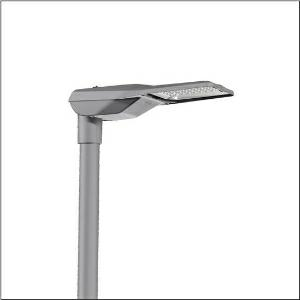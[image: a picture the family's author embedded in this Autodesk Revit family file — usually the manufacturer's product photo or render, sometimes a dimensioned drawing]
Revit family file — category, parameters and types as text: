
# Revit family: streetlight_sl_21_iq_mini___p0_8a_5xe2u31v08hb_1f16
name_source: partatom
category: Lighting Fixtures
units: mm (PartAtom-declared; Revit-internal decimal feet)

## family parameters
Cut with Voids When Loaded = No
Host = Face
Light Source = No
Part Type = Normal
Room Calculation Point = No
Round Connector Dimension = Use Diameter
Shared = No

## types (1)
- --- (1 x LED, 9830 lm, 71 W, 3000K)
    Apparent Load = 71 VA
    CIE Flux Codes = 33 69 96 100 100
    Color Rendering = 70
    Color Temperature = 3000K
    Default Elevation = 1800 mm
    Description = Streetlight SL 21 iQ mini, mast luminaire, primary light control with lens, of PMMA, primary optical cover: cover, of toughened safety glass, transparent, light distribution: P0.8a, light emission: direct distribution, primary light characteristic: asymmetric, installation type: post-top, side-entry, LED, High Power LED, rated luminous flux: 9.830lm, luminous efficacy: 139lm/W, light colour: 730, colour temperature: 3000K, control gear: iQ-Street Remote, D4i with power reduction, control: pre-setting: logarithmic dimming characteristic, Street-Remote, Auto-Match, Temp-Guard, Lumen-Switch, Night-Set, Smart-Wire, Light-Fading, Desk-Remote (wireless, voltage-free reading and setting of iQ features in the workshop via application-optimized NFC function/RFID function), optimised constant luminous flux control (CLO 2.0), mains connection: 220..240V, AC, 50/60Hz, start of lifetime: 71W, end of service life: 75W, reduction: 30W, luminaire housing, of diecast aluminium, powder-coated, Siteco® metallic grey (DB 702S), corrosivity category C5 mid according to DIN EN ISO 12944, please order mast flange separately, inclination adjustable: 0°, 5°, 10°, 15°, sealing non-destructively replaceable, multi-level sealing system, length: 628mm, width: 235mm, height: 110mm, mast flange for spigot size: 42mm (side-entry): 5XC10008XM4, 60/48mm (side-entry/post-top): 5XC10108XM2, 76/60mm (side-entry/post-top): 5XC10108XM1, mounting height: 4..8m, Smart Interface above, protection rating (complete): IP66, insulation class (complete): insulation class II (safety insulation), certification: CE, ENEC, ENEC+, VDE, impact resistance: IK10, permissible operating ambient temperature for outdoor applications: -40..+50°C, standard-compliant lighting for roads and squares, packaging unit: 1 piece

Light Distribution: P0.8a
    Height = 110 mm
    Lamp = 1 x LED
    Lamp Light Flux = 9830 lm
    Lamp Power = 71 W
    Lamp count = 1
    Length = 625 mm
    Luminous efficacy = 138 lm/W
    Manufacturer = Siteco
    ModVariant = No
    Model = 5XE2U31V08HB
    Number of Poles = 1
    OnlyDefault = Yes
    Power Factor = 1
    Product Name = Streetlight SL 21 iQ mini | P0.8a
    Product group = mast luminaire | pylon top
    ProductGroupID = 6100
    Protection Class = Protection class II
    Protection Degree = IP 66
    RLX_Detail_Level = 1
    RLX_Emergency_Light_Flux = 0 lm
    RLX_Emergency_Type = 0
    RLX_Emergency_Type_DB = No
    RlxData = <blob elided: 26237 chars, md5=596cf52c>
    Socket = socket
    Standby Power = 0 W
    System Light Flux = 9830 lm
    System Power = 71 W
    Type Comments = factory setting: luminous flux: 100 % | dim-lin: 254 | 716 mA
    Type Image = l_1003515.jpg
    URL = http://relux.com
    VarID = @adj_074100
    Voltage = 0 V
    Weight = 0.00 kg
    Width = 234 mm

## geometry (parser evidence)
native form markers: Blend x4, Sweep x10
no freeform markers — native parametric forms only
